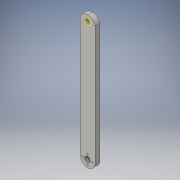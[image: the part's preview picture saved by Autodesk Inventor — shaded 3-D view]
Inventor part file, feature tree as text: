
AUTODESK INVENTOR PART (.ipt)
format: ipt  version: 2016 (Build 200138000, 138)  size: 154,624 bytes
history: native  units: in
note: dims shown in document units (in); Inventor stores cm internally (conversion verified against a paired STEP export)
features: sketch x9, extrude x5, hole x1
ambient origin geometry x8: Origin, YZ Plane, XZ Plane, XY Plane, X Axis, Y Axis, Z Axis, Center Point
bodies: Solid1 (feature_tree)
feature tree (15):
  sketch  "Sketch1"  dims[d0=0.8268in d1=0.0394in]
  sketch  "Sketch2"  dims[d2=0.0394in d3=0.0394in]
  extrude  "Extrusion1"  Depth=0.0394in
  extrude  "Extrusion2"  Depth=0.0394in
  extrude  "Extrusion3"  Depth=0.0394in
  hole  "Hole1"  [1 undecoded]
  sketch  "Sketch5"  dims[d8=0.315in d14=0.4921in]
  sketch  "Sketch6"  dims[d15=0.4921in d16=0.4921in]
  sketch  "Sketch7"  dims[d17=0.0787in]
  extrude  "Extrusion5"  Depth=0.4921in
  extrude  "Extrusion6"  Depth=0.4921in
  sketch  "Sketch3"  dims[d4=0.0394in d5=0.315in]
  sketch  "Sketch4"  dims[d6=0.315in d7=0.315in]
  sketch  "Sketch9"  dims[d18=0.0787in]
  sketch  "Sketch10"  dims[d19=0.0787in d20=0.5118in d21=0.5118in d30=7.874in d31=0.3819in d32=0.4921in d34=0.0984in d35=0.0984in d36=0.0984in d37=0.3937in d38=0.4724in d39=0.4724in d40=0.3228in d41=0.0in d42=0.3937in d43=0.0in d44=0.0787in d45=0.0in d46=0.0787in d47=0.2362in d48=0.1575in d49=0.0787in d50=90.0deg d51=0.3937in d52=0.8108in d55=0.8465in d56=0.0787in d57=0.0in d58=0.374in d59=0.3937in d60=0.0in]
note: 1 required parameter value undecoded (feature->parameter linkage not recoverable at this tier; creation-order binding heuristic only, values carry confidence <= 0.55)
